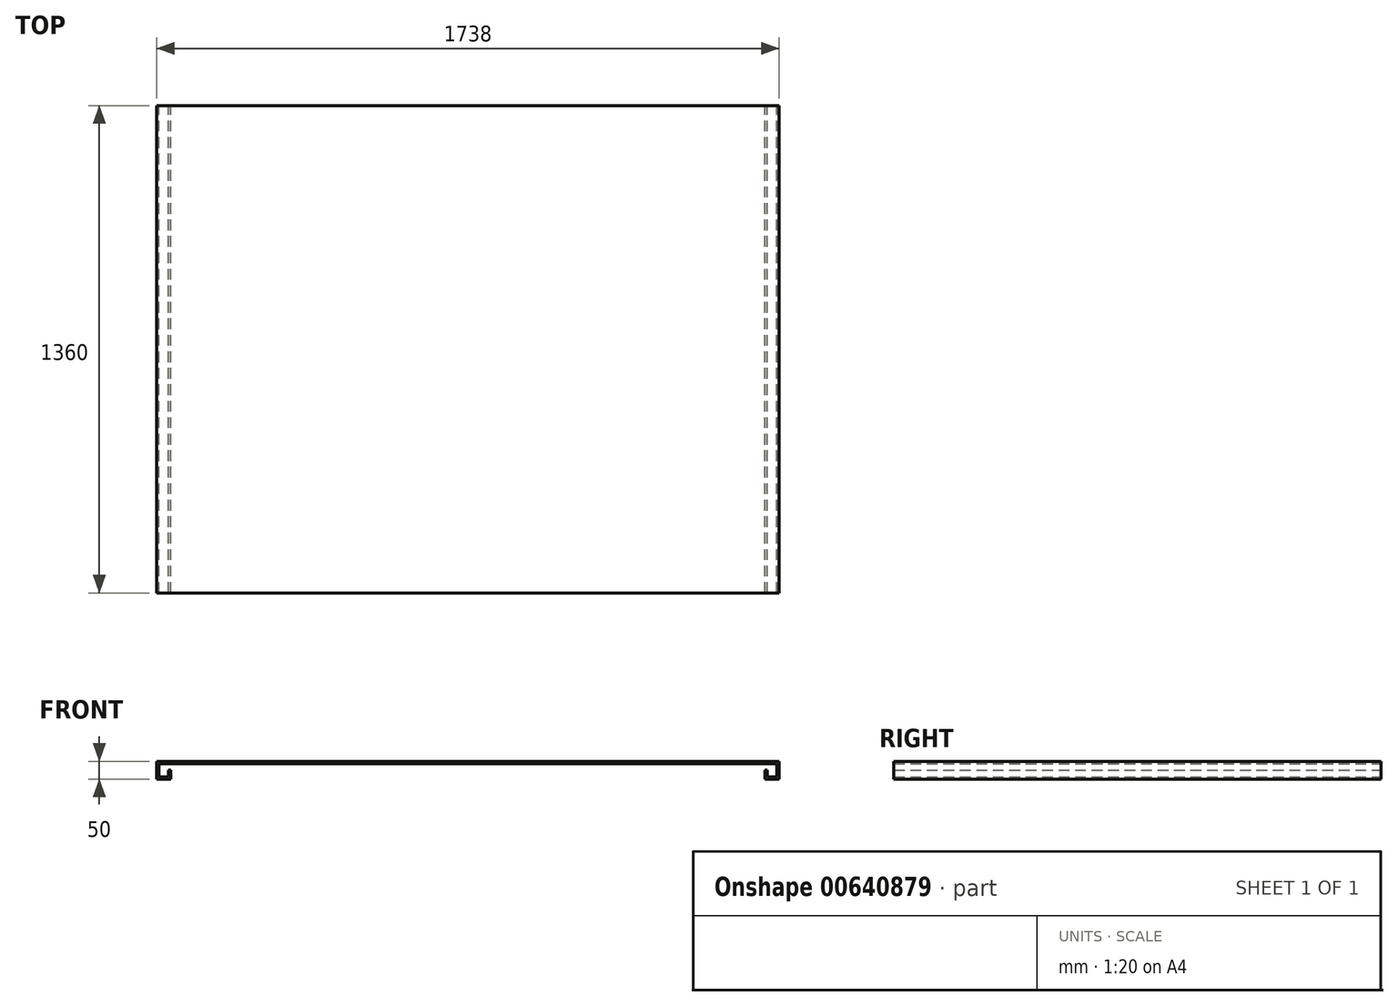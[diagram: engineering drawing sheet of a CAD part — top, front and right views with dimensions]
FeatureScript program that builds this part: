
annotation { "Feature Type Name" : "Feature", "Feature Type Description" : "" }
export const myFeature = defineFeature(function(context is Context, id is Id, definition is map)
    precondition{}
    {
        {
            var Q0;
            Q0=qCreatedBy(makeId("Front.planeOp"),FACE);
            var sketch = newSketch(context, id + "F0", { "sketchPlane" : qUnion([Q0])});
            skLineSegment(sketch, "E0", {"start": v(829, -25) * mm, "end": v(869, -25) * mm});
            skLineSegment(sketch, "E1", {"start": v(869, -25) * mm, "end": v(869, 25) * mm});
            skLineSegment(sketch, "E2", {"start": v(869, 25) * mm, "end": v(-869, 25) * mm});
            skLineSegment(sketch, "E3", {"start": v(-869, 25) * mm, "end": v(-869, -25) * mm});
            skLineSegment(sketch, "E4", {"start": v(-869, -25) * mm, "end": v(-829, -25) * mm});
            skLineSegment(sketch, "E5", {"start": v(0, 487.42) * mm, "end": v(0, -697.82) * mm, "construction": true});
            skLineSegment(sketch, "E6", {"start": v(-383.13, 0) * mm, "end": v(584.49, 0) * mm, "construction": true});
            skLineSegment(sketch, "E7", {"start": v(-829, -25) * mm, "end": v(-829, 0) * mm});
            skLineSegment(sketch, "E8", {"start": v(829, -25) * mm, "end": v(829, 0) * mm});
            skLineSegment(sketch, "E9.0", {"start": v(-835.35, -18.65) * mm, "end": v(-835.35, 0) * mm});
            skLineSegment(sketch, "E9.1", {"start": v(-862.65, -18.65) * mm, "end": v(-835.35, -18.65) * mm});
            skLineSegment(sketch, "E9.2", {"start": v(-862.65, 18.65) * mm, "end": v(-862.65, -18.65) * mm});
            skLineSegment(sketch, "E9.3", {"start": v(835.35, -18.65) * mm, "end": v(835.35, 0) * mm});
            skLineSegment(sketch, "E9.4", {"start": v(835.35, -18.65) * mm, "end": v(862.65, -18.65) * mm});
            skLineSegment(sketch, "E9.5", {"start": v(862.65, -18.65) * mm, "end": v(862.65, 18.65) * mm});
            skLineSegment(sketch, "E9.6", {"start": v(862.65, 18.65) * mm, "end": v(-862.65, 18.65) * mm});
            skLineSegment(sketch, "E10", {"start": v(-835.35, 0) * mm, "end": v(-829, 0) * mm});
            skLineSegment(sketch, "E11", {"start": v(829, 0) * mm, "end": v(835.35, 0) * mm});
            skSolve(sketch);
        }
        {
            var Q0;
            Q0 = qSketchRegion(id + "F0", true);
            extrude(context, id + "F1", {"entities" : qUnion([Q0]), "depth" : 1360 * mm, "offsetDistance" : 25.4 * mm});
        }
    });
